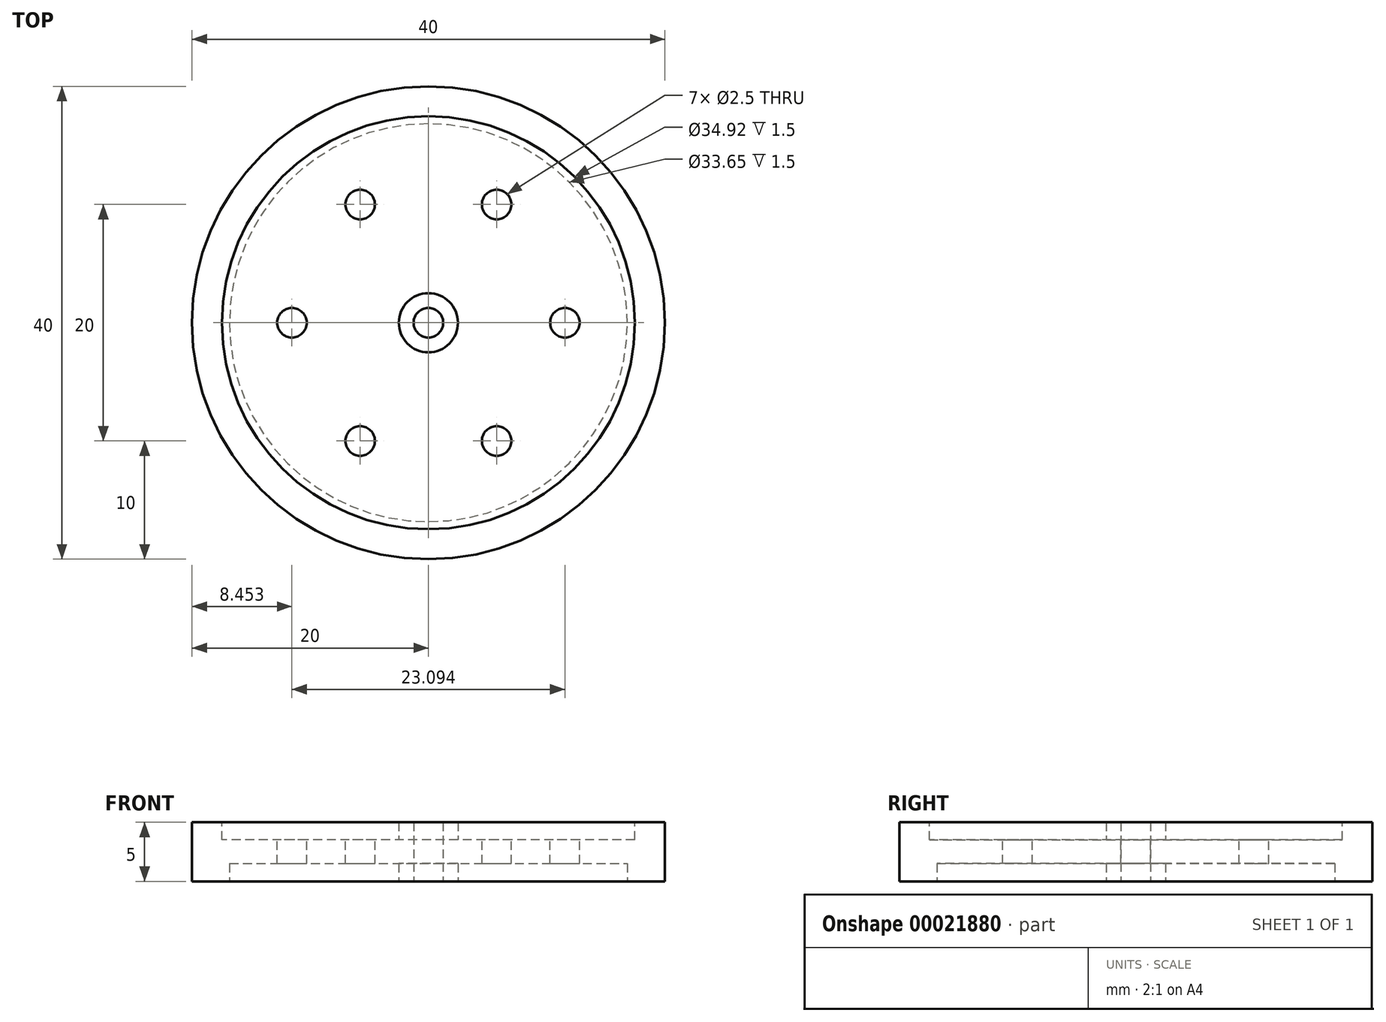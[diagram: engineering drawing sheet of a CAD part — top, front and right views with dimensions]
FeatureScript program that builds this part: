
annotation { "Feature Type Name" : "Feature", "Feature Type Description" : "" }
export const myFeature = defineFeature(function(context is Context, id is Id, definition is map)
    precondition{}
    {
        {
            var Q0;
            Q0=qCreatedBy(makeId("Top.planeOp"),FACE);
            var sketch = newSketch(context, id + "F0", { "sketchPlane" : qUnion([Q0])});
            skCircle(sketch, "E0", {"center": v(0, 0) * mm, "radius": 20 * mm});
            skSolve(sketch);
        }
        {
            var Q0;
            Q0 = qSketchRegion(id + "F0", true);
            extrude(context, id + "F1", {"entities" : qUnion([Q0]), "depth" : 5 * mm});
        }
        {
            var Q0;
            Q0=makeQuery(id+"F1.opExtrude","CAP_FACE",FACE,{"disambiguationData":[OSD([sQuery(id+"F0.wireOp",EDGE,"E0")])],"isStart":false});
            var sketch = newSketch(context, id + "F2", { "sketchPlane" : qUnion([Q0])});
            skCircle(sketch, "E1.cCircle", {"center": v(0, 0) * mm, "radius": 10 * mm, "construction": true});
            skLineSegment(sketch, "E1.0", {"start": v(-5.77, 10) * mm, "end": v(5.77, 10) * mm});
            skLineSegment(sketch, "E1.1", {"start": v(5.77, 10) * mm, "end": v(11.55, 0) * mm});
            skLineSegment(sketch, "E1.2", {"start": v(11.55, 0) * mm, "end": v(5.77, -10) * mm});
            skLineSegment(sketch, "E1.3", {"start": v(5.77, -10) * mm, "end": v(-5.77, -10) * mm});
            skLineSegment(sketch, "E1.4", {"start": v(-5.77, -10) * mm, "end": v(-11.55, 0) * mm});
            skLineSegment(sketch, "E1.5", {"start": v(-11.55, 0) * mm, "end": v(-5.77, 10) * mm});
            skPoint(sketch, "E1.0.midPoint", {"position": v(0, 10) * mm});
            skSolve(sketch);
        }
        {
            var Q0;
            Q0=sQuery(id+"F2.wireOp",VERTEX,"E1.0.start");
            var Q1;
            Q1=sQuery(id+"F2.wireOp",VERTEX,"E1.1.start");
            var Q2;
            Q2=sQuery(id+"F2.wireOp",VERTEX,"E1.2.start");
            var Q3;
            Q3=sQuery(id+"F2.wireOp",VERTEX,"E1.3.start");
            var Q4;
            Q4=sQuery(id+"F2.wireOp",VERTEX,"E1.4.start");
            var Q5;
            Q5=sQuery(id+"F2.wireOp",VERTEX,"E1.5.start");
            var Q6;
            Q6=makeQuery(id+"F1.opExtrude","SWEPT_BODY",BODY,{"disambiguationData":[OSD([sQuery(id+"F0.wireOp",EDGE,"E0")])]});
            hole(context, id + "F3", {"style" : HoleStyle.SIMPLE, "holeDiameter" : 2.5 * mm, "endStyle" : HoleEndStyle.THROUGH, "locations" : qUnion([Q0, Q1, Q2, Q3, Q4, Q5]), "scope" : qUnion([Q6])});
        }
        {
            var Q0;
            Q0=qCreatedBy(makeId("Top.planeOp"),FACE);
            var sketch = newSketch(context, id + "F4", { "sketchPlane" : qUnion([Q0])});
            skCircle(sketch, "E2", {"center": v(0, 0) * mm, "radius": 2.5 * mm});
            skSolve(sketch);
        }
        {
            var Q0;
            Q0=makeQuery(id+"F1.opExtrude","CAP_FACE",FACE,{"disambiguationData":[OSD([sQuery(id+"F0.wireOp",EDGE,"E0")])],"isStart":false});
            var sketch = newSketch(context, id + "F5", { "sketchPlane" : qUnion([Q0])});
            skCircle(sketch, "E3", {"center": v(0, 0) * mm, "radius": 17.46 * mm});
            skSolve(sketch);
        }
        {
            var Q0;
            Q0 = qSketchRegion(id + "F5", true);
            extrude(context, id + "F6", {"entities" : qUnion([Q0]), "operationType" : NewBodyOperationType.REMOVE, "oppositeDirection" : true, "depth" : 1.5 * mm});
        }
        {
            var Q0;
            Q0=makeQuery(id+"F6.boolean.opBoolean","COPY",FACE,{"derivedFrom":makeQuery(id+"F6.opExtrude","CAP_FACE",FACE,{"disambiguationData":[OSD([sQuery(id+"F5.wireOp",EDGE,"E3")])],"isStart":false})});
            var sketch = newSketch(context, id + "F7", { "sketchPlane" : qUnion([Q0])});
            skCircle(sketch, "E4", {"center": v(-5.77, 10) * mm, "radius": 2.5 * mm});
            skSolve(sketch);
        }
        {
            var Q0;
            Q0=makeQuery(id+"F1.opExtrude","CAP_FACE",FACE,{"disambiguationData":[OSD([sQuery(id+"F0.wireOp",EDGE,"E0")])],"isStart":true});
            var sketch = newSketch(context, id + "F8", { "sketchPlane" : qUnion([Q0])});
            skCircle(sketch, "E5", {"center": v(0, 0) * mm, "radius": 16.83 * mm});
            skSolve(sketch);
        }
        {
            var Q0;
            Q0 = qSketchRegion(id + "F8", true);
            extrude(context, id + "F9", {"entities" : qUnion([Q0]), "operationType" : NewBodyOperationType.REMOVE, "oppositeDirection" : true, "depth" : 1.5 * mm});
        }
        {
            var Q0;
            Q0=makeQuery(id+"F4.imprint","IMPRINT",FACE,{"disambiguationData":[TD([[makeQuery(id+"F4.imprint","IMPRINT",EDGE,{"derivedFrom":sQuery(id+"F4.wireOp",EDGE,"E2")}),1.0]])]});
            var sketch = newSketch(context, id + "F10", { "sketchPlane" : qUnion([Q0])});
            skCircle(sketch, "E6", {"center": v(0, 0) * mm, "radius": 1.25 * mm});
            skSolve(sketch);
        }
        {
            var Q0;
            Q0 = qSketchRegion(id + "F10", true);
            extrude(context, id + "F11", {"entities" : qUnion([Q0]), "operationType" : NewBodyOperationType.REMOVE, "depth" : 25.4 * mm});
        }
        {
            var Q0;
            Q0=makeQuery(id+"F4.imprint","IMPRINT",FACE,{"disambiguationData":[TD([[makeQuery(id+"F4.imprint","IMPRINT",EDGE,{"derivedFrom":sQuery(id+"F4.wireOp",EDGE,"E2")}),1.0]])]});
            extrude(context, id + "F12", {"entities" : qUnion([Q0]), "operationType" : NewBodyOperationType.ADD, "depth" : 1.5 * mm});
        }
        {
            var Q0;
            Q0=makeQuery(id+"F7.imprint","IMPRINT",FACE,{"disambiguationData":[TD([[makeQuery(id+"F7.imprint","IMPRINT",EDGE,{"derivedFrom":sQuery(id+"F7.wireOp",EDGE,"E4")}),-1.0]])]});
            var sketch = newSketch(context, id + "F13", { "sketchPlane" : qUnion([Q0])});
            skCircle(sketch, "E7", {"center": v(0, 0) * mm, "radius": 2.5 * mm});
            skSolve(sketch);
        }
        {
            var Q0;
            Q0 = qSketchRegion(id + "F13", true);
            extrude(context, id + "F14", {"entities" : qUnion([Q0]), "operationType" : NewBodyOperationType.ADD, "depth" : 1.5 * mm});
        }
        {
            var Q0;
            Q0=makeQuery(id+"F14.opExtrude","CAP_FACE",FACE,{"disambiguationData":[OSD([sQuery(id+"F13.wireOp",EDGE,"E7")])],"isStart":false});
            var sketch = newSketch(context, id + "F15", { "sketchPlane" : qUnion([Q0])});
            skPoint(sketch, "E8", {"position": v(0, 0) * mm});
            skSolve(sketch);
        }
        {
            var Q0;
            Q0=sQuery(id+"F15.wireOp",VERTEX,"E8");
            var Q1;
            Q1=makeQuery(id+"F1.opExtrude","SWEPT_BODY",BODY,{"disambiguationData":[OSD([sQuery(id+"F0.wireOp",EDGE,"E0")])]});
            hole(context, id + "F16", {"style" : HoleStyle.SIMPLE, "holeDiameter" : 2.5 * mm, "endStyle" : HoleEndStyle.THROUGH, "locations" : qUnion([Q0]), "scope" : qUnion([Q1])});
        }
    });
